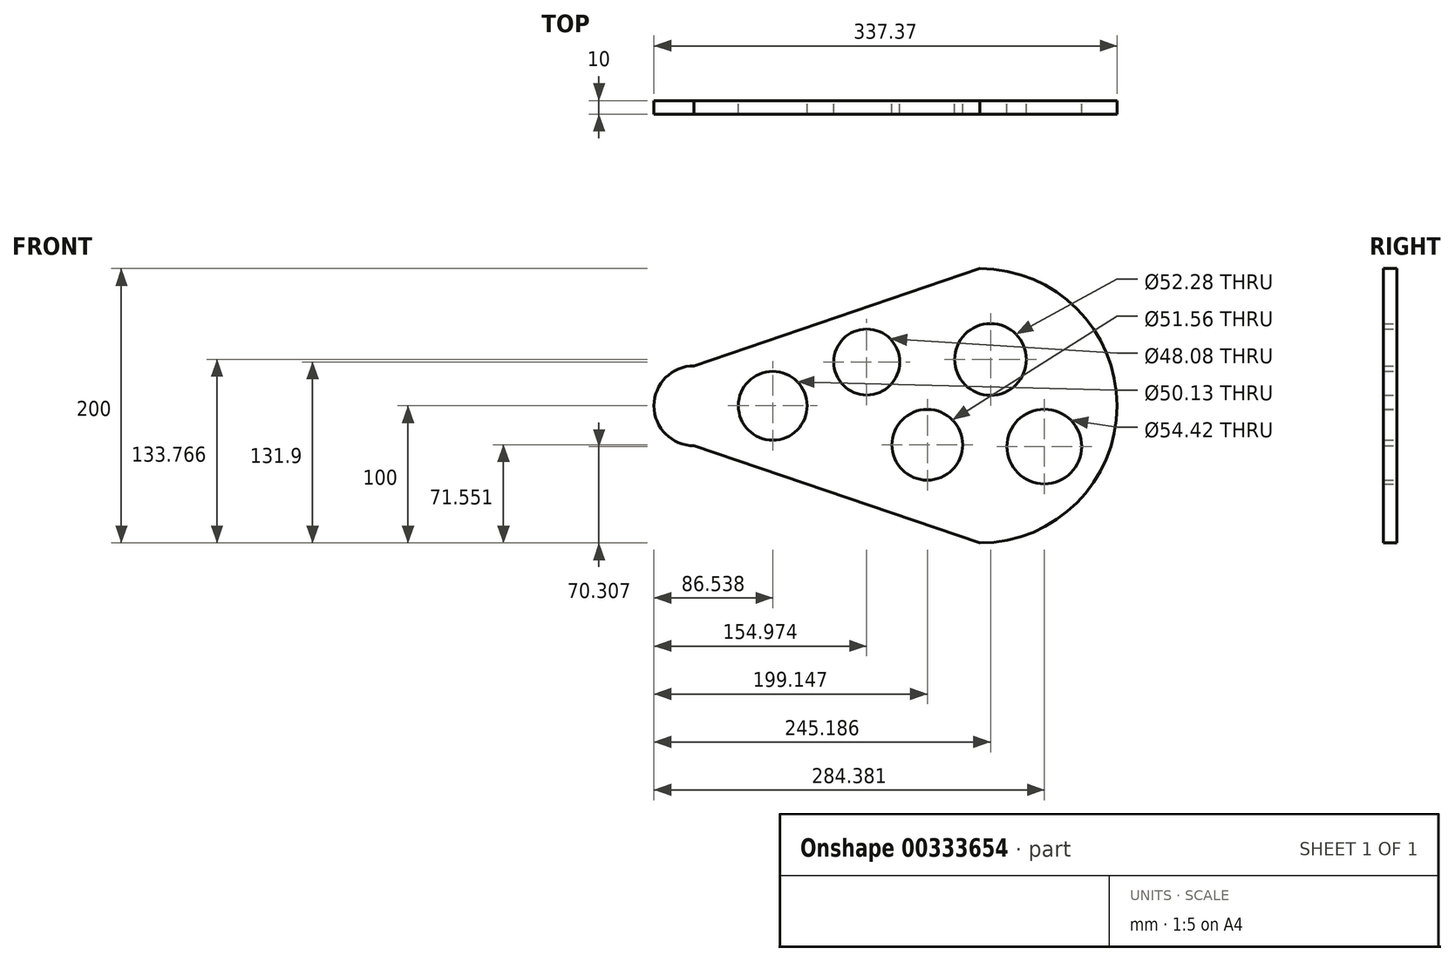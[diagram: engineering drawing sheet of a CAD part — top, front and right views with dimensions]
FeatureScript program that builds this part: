
annotation { "Feature Type Name" : "Feature", "Feature Type Description" : "" }
export const myFeature = defineFeature(function(context is Context, id is Id, definition is map)
    precondition{}
    {
        {
            var Q0;
            Q0=qCreatedBy(makeId("Front.planeOp"),FACE);
            var sketch = newSketch(context, id + "F0", { "sketchPlane" : qUnion([Q0])});
            skArc(sketch, "E0", {"start": v(0, -100) * mm, "mid": v(100, 0) * mm, "end": v(0, 100) * mm});
            skArc(sketch, "E1", {"start": v(-208.25, 29.12) * mm, "mid": v(-237.37, 0) * mm, "end": v(-208.25, -29.12) * mm});
            skLineSegment(sketch, "E2", {"start": v(-208.25, 29.12) * mm, "end": v(0, 100) * mm});
            skLineSegment(sketch, "E3", {"start": v(-208.25, -29.12) * mm, "end": v(0, -100) * mm});
            skCircle(sketch, "E4", {"center": v(-150.83, 0) * mm, "radius": 25.06 * mm});
            skCircle(sketch, "E5", {"center": v(-82.4, 31.9) * mm, "radius": 24.04 * mm});
            skCircle(sketch, "E6", {"center": v(-38.22, -28.45) * mm, "radius": 25.78 * mm});
            skCircle(sketch, "E7", {"center": v(7.82, 33.77) * mm, "radius": 26.14 * mm});
            skCircle(sketch, "E8", {"center": v(47.01, -29.7) * mm, "radius": 27.21 * mm});
            skSolve(sketch);
        }
        {
            var Q0;
            Q0 = qSketchRegion(id + "F0", true);
            extrude(context, id + "F1", {"entities" : qUnion([Q0]), "depth" : 10 * mm});
        }
    });
